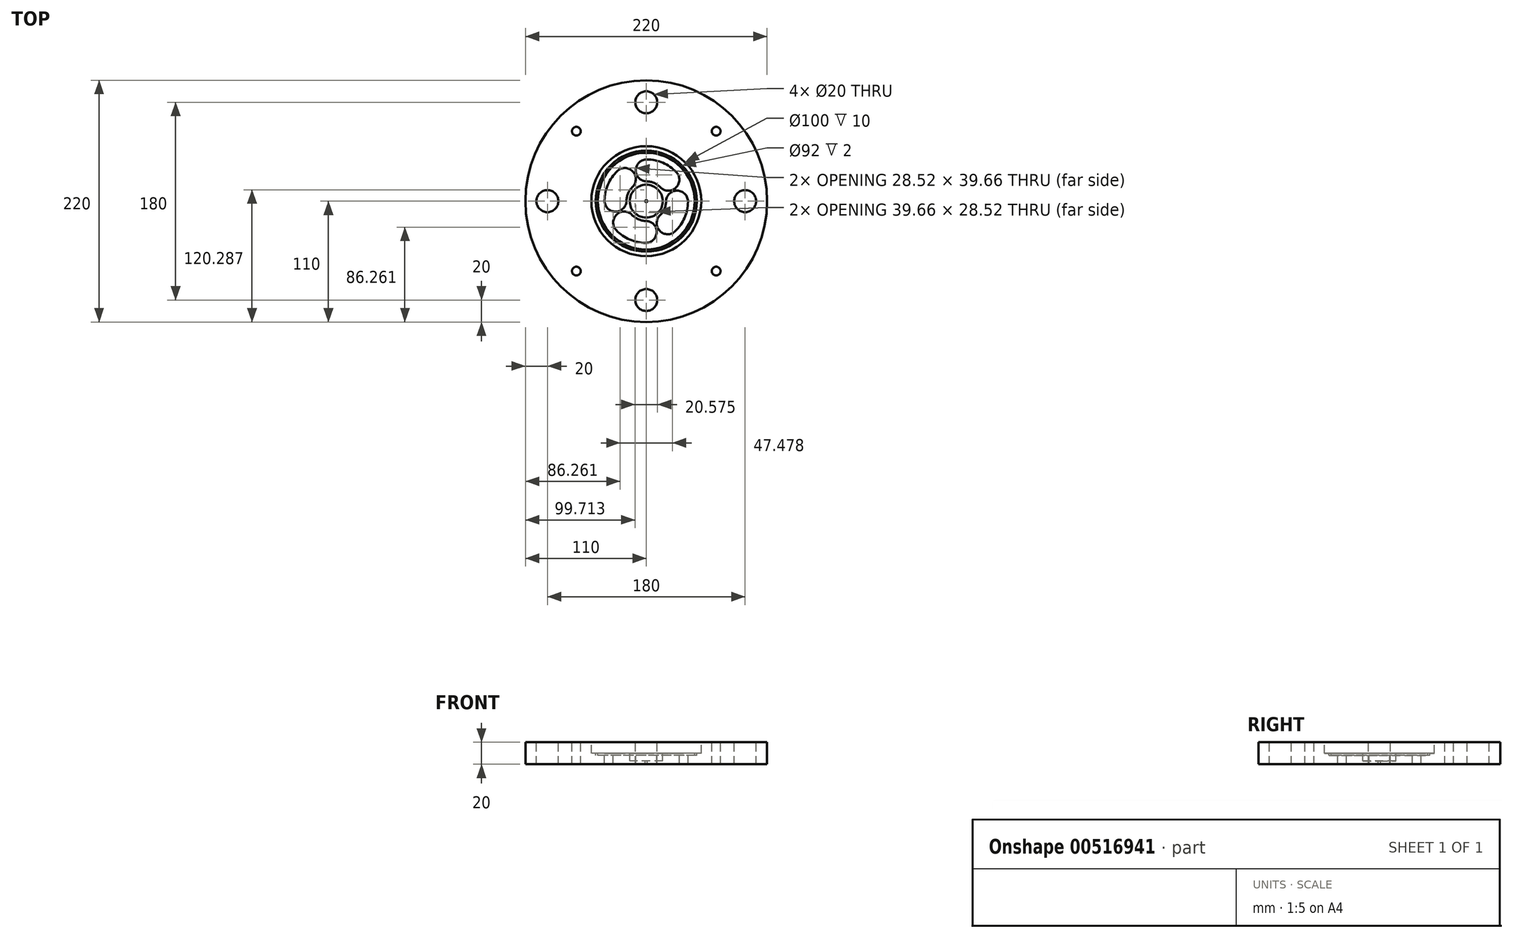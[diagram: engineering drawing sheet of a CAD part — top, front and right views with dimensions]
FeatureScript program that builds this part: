
annotation { "Feature Type Name" : "Feature", "Feature Type Description" : "" }
export const myFeature = defineFeature(function(context is Context, id is Id, definition is map)
    precondition{}
    {
        {
            var Q0;
            Q0=qCreatedBy(makeId("Front.planeOp"),FACE);
            var sketch = newSketch(context, id + "F0", { "sketchPlane" : qUnion([Q0])});
            skLineSegment(sketch, "E0", {"start": v(0, 0) * mm, "end": v(0, -20) * mm});
            skLineSegment(sketch, "E1", {"start": v(0, -20) * mm, "end": v(110, -20) * mm});
            skLineSegment(sketch, "E2", {"start": v(110, -20) * mm, "end": v(110, 0) * mm});
            skLineSegment(sketch, "E3", {"start": v(110, 0) * mm, "end": v(0, 0) * mm});
            skSolve(sketch);
        }
        {
            var Q0;
            Q0=makeQuery(id+"F0.imprint","IMPRINT",FACE,{"disambiguationData":[TD([[makeQuery(id+"F0.imprint","IMPRINT",EDGE,{"derivedFrom":sQuery(id+"F0.wireOp",EDGE,"E0")}),1.0]])]});
            var Q1;
            Q1=sQuery(id+"F0.wireOp",EDGE,"E0");
            revolve(context, id + "F1", {"entities" : qUnion([Q0]), "axis" : qUnion([Q1]), "revolveType" : RevolveType.FULL});
        }
        {
            var Q0;
            Q0=makeQuery(id+"F1.opRevolve","SWEPT_FACE",FACE,{"disambiguationData":[OSD([sQuery(id+"F0.wireOp",EDGE,"E3")])]});
            cPlane(context, id + "F2", {"entities" : qUnion([Q0]), "cplaneType" : CPlaneType.OFFSET, "offset" : 10 * mm, "oppositeDirection" : true, "width" : 150 * mm, "height" : 150 * mm});
        }
        {
            var Q0;
            Q0=qCreatedBy(makeId("Top.planeOp"),FACE);
            var sketch = newSketch(context, id + "F3", { "sketchPlane" : qUnion([Q0])});
            skLineSegment(sketch, "E4", {"start": v(0, 0) * mm, "end": v(0, 90) * mm});
            skLineSegment(sketch, "E5", {"start": v(0, 0) * mm, "end": v(90, 0) * mm});
            skLineSegment(sketch, "E6", {"start": v(0, 0) * mm, "end": v(0, -90) * mm});
            skLineSegment(sketch, "E7", {"start": v(0, 0) * mm, "end": v(-90, 0) * mm});
            skPoint(sketch, "E8", {"position": v(0, 90) * mm});
            skPoint(sketch, "E9", {"position": v(90, 0) * mm});
            skPoint(sketch, "E10", {"position": v(0, -90) * mm});
            skPoint(sketch, "E11", {"position": v(-90, 0) * mm});
            skSolve(sketch);
        }
        {
            var Q0;
            Q0=sQuery(id+"F3.wireOp",VERTEX,"E8");
            var Q1;
            Q1=sQuery(id+"F3.wireOp",VERTEX,"E9");
            var Q2;
            Q2=sQuery(id+"F3.wireOp",VERTEX,"E10");
            var Q3;
            Q3=sQuery(id+"F3.wireOp",VERTEX,"E11");
            var Q4;
            Q4=makeQuery(id+"F1.opRevolve","SWEPT_BODY",BODY,{"disambiguationData":[OSD([sQuery(id+"F0.wireOp",EDGE,"E0"),sQuery(id+"F0.wireOp",EDGE,"E1"),sQuery(id+"F0.wireOp",EDGE,"E2"),sQuery(id+"F0.wireOp",EDGE,"E3")])]});
            hole(context, id + "F4", {"style" : HoleStyle.C_SINK, "endStyle" : HoleEndStyle.BLIND, "holeDiameter" : 20 * mm, "cSinkDiameter" : 20 * mm, "cSinkAngle" : 90 * degree, "holeDepth" : 20 * mm, "isTappedThrough" : true, "tappedDepth" : 12 * mm, "tapClearance" : 3, "startFromSketch" : true, "locations" : qUnion([Q0, Q1, Q2, Q3]), "scope" : qUnion([Q4])});
        }
        {
            var Q0;
            Q0=qCreatedBy(makeId("Top.planeOp"),FACE);
            var sketch = newSketch(context, id + "F5", { "sketchPlane" : qUnion([Q0])});
            skCircle(sketch, "E12", {"center": v(0, 0) * mm, "radius": 50 * mm});
            skSolve(sketch);
        }
        {
            var Q0;
            Q0=makeQuery(id+"F5.imprint","IMPRINT",FACE,{"disambiguationData":[TD([[makeQuery(id+"F5.imprint","IMPRINT",EDGE,{"derivedFrom":sQuery(id+"F5.wireOp",EDGE,"E12")}),1.0]])]});
            extrude(context, id + "F6", {"entities" : qUnion([Q0]), "operationType" : NewBodyOperationType.REMOVE, "oppositeDirection" : true, "depth" : 10 * mm, "offsetDistance" : 25 * mm});
        }
        {
            var Q0;
            Q0=qCreatedBy(makeId("Top.planeOp"),FACE);
            var sketch = newSketch(context, id + "F7", { "sketchPlane" : qUnion([Q0])});
            skCircle(sketch, "E13", {"center": v(0, 0) * mm, "radius": 15 * mm});
            skSolve(sketch);
        }
        {
            var Q0;
            Q0=makeQuery(id+"F7.imprint","IMPRINT",FACE,{"disambiguationData":[TD([[makeQuery(id+"F7.imprint","IMPRINT",EDGE,{"derivedFrom":sQuery(id+"F7.wireOp",EDGE,"E13")}),1.0]])]});
            extrude(context, id + "F8", {"entities" : qUnion([Q0]), "operationType" : NewBodyOperationType.REMOVE, "oppositeDirection" : true, "depth" : 17 * mm, "offsetDistance" : 25 * mm});
        }
        {
            var Q0;
            Q0=qCreatedBy(makeId("Top.planeOp"),FACE);
            var sketch = newSketch(context, id + "F9", { "sketchPlane" : qUnion([Q0])});
            skCircle(sketch, "E14", {"center": v(0, 0) * mm, "radius": 1 * mm});
            skSolve(sketch);
        }
        {
            var Q0;
            Q0=makeQuery(id+"F9.imprint","IMPRINT",FACE,{"disambiguationData":[TD([[makeQuery(id+"F9.imprint","IMPRINT",EDGE,{"derivedFrom":sQuery(id+"F9.wireOp",EDGE,"E14")}),1.0]])]});
            extrude(context, id + "F10", {"entities" : qUnion([Q0]), "operationType" : NewBodyOperationType.REMOVE, "oppositeDirection" : true, "depth" : 20 * mm, "offsetDistance" : 25 * mm});
        }
        {
            var Q0;
            Q0=qCreatedBy(id+"F2.planeOp",FACE);
            var sketch = newSketch(context, id + "F11", { "sketchPlane" : qUnion([Q0])});
            skCircle(sketch, "E15", {"center": v(0, 0) * mm, "radius": 40 * mm});
            skArc(sketch, "E16", {"start": v(-26.43, 27.3) * mm, "mid": v(-34.87, 15.11) * mm, "end": v(-38, 0.62) * mm});
            skLineSegment(sketch, "E17", {"start": v(27.3, 26.43) * mm, "end": v(27.3, 26.43) * mm});
            skArc(sketch, "E18", {"start": v(26.43, -27.3) * mm, "mid": v(34.87, -15.11) * mm, "end": v(38, -0.62) * mm});
            skLineSegment(sketch, "E19", {"start": v(-27.3, -26.43) * mm, "end": v(-27.3, -26.43) * mm});
            skArc(sketch, "E20", {"start": v(12.94, 12.52) * mm, "mid": v(7.16, 16.52) * mm, "end": v(0.3, 18) * mm});
            skArc(sketch, "E21", {"start": v(12.52, -12.94) * mm, "mid": v(16.52, -7.16) * mm, "end": v(18, -0.3) * mm});
            skArc(sketch, "E22", {"start": v(-12.94, -12.52) * mm, "mid": v(-7.16, -16.52) * mm, "end": v(-0.3, -18) * mm});
            skArc(sketch, "E23", {"start": v(-12.52, 12.94) * mm, "mid": v(-16.52, 7.16) * mm, "end": v(-18, 0.3) * mm});
            skArc(sketch, "E24", {"start": v(-12.52, 12.94) * mm, "mid": v(-12.3, 27.08) * mm, "end": v(-26.43, 27.3) * mm});
            skArc(sketch, "E25", {"start": v(-38, 0.62) * mm, "mid": v(-28.16, -9.54) * mm, "end": v(-18, 0.3) * mm});
            skLineSegment(sketch, "E26", {"start": v(0.3, 18) * mm, "end": v(0.3, 18) * mm});
            skLineSegment(sketch, "E27", {"start": v(0.62, 38) * mm, "end": v(0.62, 38) * mm});
            skArc(sketch, "E28", {"start": v(27.3, 26.43) * mm, "mid": v(15.11, 34.87) * mm, "end": v(0.62, 38) * mm});
            skArc(sketch, "E29", {"start": v(12.94, 12.52) * mm, "mid": v(27.08, 12.3) * mm, "end": v(27.3, 26.43) * mm});
            skArc(sketch, "E30", {"start": v(38, -0.62) * mm, "mid": v(28.16, 9.54) * mm, "end": v(18, -0.3) * mm});
            skArc(sketch, "E31", {"start": v(12.52, -12.94) * mm, "mid": v(12.3, -27.08) * mm, "end": v(26.43, -27.3) * mm});
            skArc(sketch, "E32", {"start": v(-0.62, -38) * mm, "mid": v(9.54, -28.16) * mm, "end": v(-0.3, -18) * mm});
            skArc(sketch, "E33", {"start": v(-27.3, -26.43) * mm, "mid": v(-15.11, -34.87) * mm, "end": v(-0.62, -38) * mm});
            skArc(sketch, "E34", {"start": v(0.62, 38) * mm, "mid": v(-9.54, 28.16) * mm, "end": v(0.3, 18) * mm});
            skArc(sketch, "E35", {"start": v(-12.94, -12.52) * mm, "mid": v(-27.08, -12.3) * mm, "end": v(-27.3, -26.43) * mm});
            skSolve(sketch);
        }
        {
            var Q0;
            Q0=makeQuery(id+"F11.imprint","IMPRINT",FACE,{"disambiguationData":[TD([[makeQuery(id+"F11.imprint","IMPRINT",EDGE,{"derivedFrom":sQuery(id+"F11.wireOp",EDGE,"E16")}),1.0]])]});
            var Q1;
            Q1=makeQuery(id+"F11.imprint","IMPRINT",FACE,{"disambiguationData":[TD([[makeQuery(id+"F11.imprint","IMPRINT",EDGE,{"derivedFrom":sQuery(id+"F11.wireOp",EDGE,"E20")}),-1.0]])]});
            var Q2;
            Q2=makeQuery(id+"F11.imprint","IMPRINT",FACE,{"disambiguationData":[TD([[makeQuery(id+"F11.imprint","IMPRINT",EDGE,{"derivedFrom":sQuery(id+"F11.wireOp",EDGE,"E18")}),1.0]])]});
            var Q3;
            Q3=makeQuery(id+"F11.imprint","IMPRINT",FACE,{"disambiguationData":[TD([[makeQuery(id+"F11.imprint","IMPRINT",EDGE,{"derivedFrom":sQuery(id+"F11.wireOp",EDGE,"E22")}),-1.0]])]});
            extrude(context, id + "F12", {"entities" : qUnion([Q0, Q1, Q2, Q3]), "operationType" : NewBodyOperationType.REMOVE, "oppositeDirection" : true, "depth" : 25 * mm, "offsetDistance" : 25 * mm});
        }
        {
            var Q0;
            Q0=qCreatedBy(makeId("Top.planeOp"),FACE);
            var sketch = newSketch(context, id + "F13", { "sketchPlane" : qUnion([Q0])});
            skLineSegment(sketch, "E36", {"start": v(0, 0) * mm, "end": v(90, 0) * mm});
            skCircle(sketch, "E37", {"center": v(63.64, 63.64) * mm, "radius": 4 * mm});
            skCircle(sketch, "E38", {"center": v(63.64, -63.64) * mm, "radius": 4 * mm});
            skCircle(sketch, "E39", {"center": v(-63.64, -63.64) * mm, "radius": 4 * mm});
            skCircle(sketch, "E40", {"center": v(-63.64, 63.64) * mm, "radius": 4 * mm});
            skPoint(sketch, "E41.orphan", {"position": v(0, 90) * mm});
            skSolve(sketch);
        }
        {
            var Q0;
            Q0=makeQuery(id+"F13.imprint","IMPRINT",FACE,{"disambiguationData":[TD([[makeQuery(id+"F13.imprint","IMPRINT",EDGE,{"derivedFrom":sQuery(id+"F13.wireOp",EDGE,"E37")}),1.0]])]});
            var Q1;
            Q1=makeQuery(id+"F13.imprint","IMPRINT",FACE,{"disambiguationData":[TD([[makeQuery(id+"F13.imprint","IMPRINT",EDGE,{"derivedFrom":sQuery(id+"F13.wireOp",EDGE,"E40")}),1.0]])]});
            var Q2;
            Q2=makeQuery(id+"F13.imprint","IMPRINT",FACE,{"disambiguationData":[TD([[makeQuery(id+"F13.imprint","IMPRINT",EDGE,{"derivedFrom":sQuery(id+"F13.wireOp",EDGE,"E39")}),1.0]])]});
            var Q3;
            Q3=makeQuery(id+"F13.imprint","IMPRINT",FACE,{"disambiguationData":[TD([[makeQuery(id+"F13.imprint","IMPRINT",EDGE,{"derivedFrom":sQuery(id+"F13.wireOp",EDGE,"E38")}),1.0]])]});
            extrude(context, id + "F14", {"entities" : qUnion([Q0, Q1, Q2, Q3]), "operationType" : NewBodyOperationType.REMOVE, "oppositeDirection" : true, "depth" : 25 * mm, "offsetDistance" : 25 * mm});
        }
        {
            var Q0;
            Q0=makeQuery(id+"F6.boolean.opBoolean","COPY",FACE,{"derivedFrom":makeQuery(id+"F6.opExtrude","CAP_FACE",FACE,{"disambiguationData":[OSD([sQuery(id+"F5.wireOp",EDGE,"E12")])],"isStart":false})});
            var sketch = newSketch(context, id + "F15", { "sketchPlane" : qUnion([Q0])});
            skCircle(sketch, "E42", {"center": v(0, 0) * mm, "radius": 44 * mm});
            skCircle(sketch, "E43", {"center": v(0, 0) * mm, "radius": 46 * mm});
            skSolve(sketch);
        }
        {
            var Q0;
            Q0=makeQuery(id+"F15.imprint","IMPRINT",FACE,{"disambiguationData":[TD([[makeQuery(id+"F15.imprint","IMPRINT",EDGE,{"derivedFrom":sQuery(id+"F15.wireOp",EDGE,"E42")}),-1.0]])]});
            extrude(context, id + "F16", {"entities" : qUnion([Q0]), "operationType" : NewBodyOperationType.REMOVE, "oppositeDirection" : true, "depth" : 2 * mm, "offsetDistance" : 25 * mm});
        }
    });
